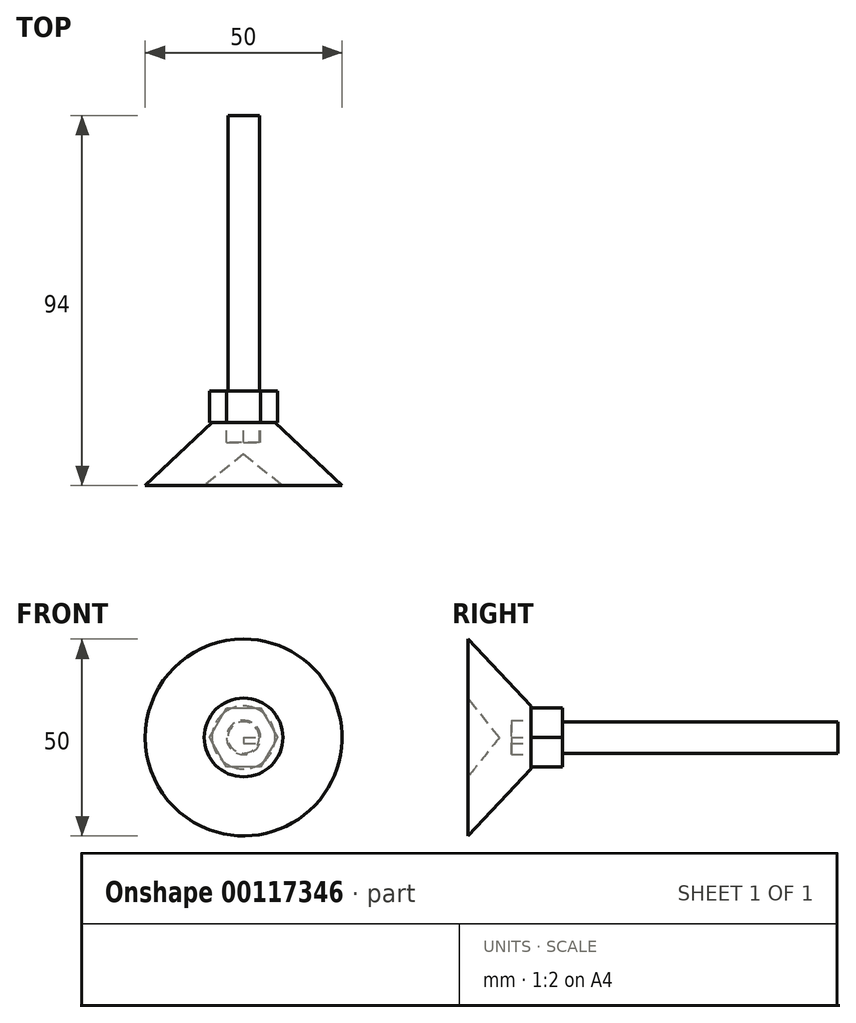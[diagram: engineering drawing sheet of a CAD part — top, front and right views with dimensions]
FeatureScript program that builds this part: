
annotation { "Feature Type Name" : "Feature", "Feature Type Description" : "" }
export const myFeature = defineFeature(function(context is Context, id is Id, definition is map)
    precondition{}
    {
        {
            var Q0;
            Q0=qCreatedBy(makeId("Front.planeOp"),FACE);
            var sketch = newSketch(context, id + "F0", { "sketchPlane" : qUnion([Q0])});
            skCircle(sketch, "E0", {"center": v(0, 0) * mm, "radius": 4 * mm});
            skSolve(sketch);
        }
        {
            var Q0;
            Q0 = qSketchRegion(id + "F0", true);
            extrude(context, id + "F1", {"entities" : qUnion([Q0]), "depth" : 70 * mm});
        }
        {
            var Q0;
            Q0=makeQuery(id+"F1.opExtrude","CAP_FACE",FACE,{"disambiguationData":[OSD([sQuery(id+"F0.wireOp",EDGE,"E0")])],"isStart":false});
            var sketch = newSketch(context, id + "F2", { "sketchPlane" : qUnion([Q0])});
            skCircle(sketch, "E1.cCircle", {"center": v(0, 0) * mm, "radius": 7.5 * mm, "construction": true});
            skLineSegment(sketch, "E1.0", {"start": v(8.66, 0.01) * mm, "end": v(4.34, -7.5) * mm});
            skLineSegment(sketch, "E1.1", {"start": v(4.34, -7.5) * mm, "end": v(-4.32, -7.5) * mm});
            skLineSegment(sketch, "E1.2", {"start": v(-4.32, -7.5) * mm, "end": v(-8.66, -0.01) * mm});
            skLineSegment(sketch, "E1.3", {"start": v(-8.66, -0.01) * mm, "end": v(-4.34, 7.5) * mm});
            skLineSegment(sketch, "E1.4", {"start": v(-4.34, 7.5) * mm, "end": v(4.32, 7.5) * mm});
            skLineSegment(sketch, "E1.5", {"start": v(4.32, 7.5) * mm, "end": v(8.66, 0.01) * mm});
            skPoint(sketch, "E1.0.midPoint", {"position": v(6.5, -3.74) * mm});
            skSolve(sketch);
        }
        {
            var Q0;
            Q0 = qSketchRegion(id + "F2", true);
            extrude(context, id + "F3", {"entities" : qUnion([Q0]), "operationType" : NewBodyOperationType.ADD, "depth" : 8 * mm});
        }
        {
            var Q0;
            Q0=makeQuery(id+"F3.opExtrude","CAP_FACE",FACE,{"disambiguationData":[OSD([sQuery(id+"F2.wireOp",EDGE,"E1.0"),sQuery(id+"F2.wireOp",EDGE,"E1.1"),sQuery(id+"F2.wireOp",EDGE,"E1.2"),sQuery(id+"F2.wireOp",EDGE,"E1.3"),sQuery(id+"F2.wireOp",EDGE,"E1.4"),sQuery(id+"F2.wireOp",EDGE,"E1.5")])],"isStart":false});
            var sketch = newSketch(context, id + "F4", { "sketchPlane" : qUnion([Q0])});
            skLineSegment(sketch, "E2.bottom", {"start": v(0, 0) * mm, "end": v(4.34, 0) * mm});
            skLineSegment(sketch, "E2.top", {"start": v(0, -1.5) * mm, "end": v(4.34, -1.5) * mm});
            skLineSegment(sketch, "E2.left", {"start": v(0, 0) * mm, "end": v(0, -1.5) * mm});
            skLineSegment(sketch, "E2.right", {"start": v(4.34, 0) * mm, "end": v(4.34, -1.5) * mm});
            skSolve(sketch);
        }
        {
            var Q0;
            Q0 = qSketchRegion(id + "F4", true);
            extrude(context, id + "F5", {"entities" : qUnion([Q0]), "operationType" : NewBodyOperationType.ADD, "depth" : 5 * mm});
        }
        {
            var Q0;
            Q0=makeQuery(id+"F5.opExtrude","SWEPT_FACE",FACE,{"disambiguationData":[OSD([sQuery(id+"F4.wireOp",EDGE,"E2.bottom")])]});
            var sketch = newSketch(context, id + "F6", { "sketchPlane" : qUnion([Q0])});
            skLineSegment(sketch, "E3", {"start": v(0, -78) * mm, "end": v(0, -94) * mm});
            skLineSegment(sketch, "E4", {"start": v(0, -78) * mm, "end": v(8, -78) * mm});
            skLineSegment(sketch, "E5", {"start": v(8, -78) * mm, "end": v(25, -94) * mm});
            skLineSegment(sketch, "E6", {"start": v(25, -94) * mm, "end": v(10, -94) * mm});
            skLineSegment(sketch, "E7", {"start": v(0, -86) * mm, "end": v(10, -94) * mm});
            skLineSegment(sketch, "E8", {"start": v(0, -86) * mm, "end": v(0, -78) * mm});
            skSolve(sketch);
        }
        {
            var Q0;
            {var subQ1=sQuery(id+"F6.wireOp",EDGE,"E5");Q0=makeQuery(id+"F6.imprint","IMPRINT",FACE,{"disambiguationData":[TD([[makeQuery(id+"F6.imprint","IMPRINT",EDGE,{"derivedFrom":subQ1}),-1.0]])]});}
            var Q1;
            Q1=sQuery(id+"F6.wireOp",EDGE,"E3");
            revolve(context, id + "F7", {"operationType" : NewBodyOperationType.ADD, "entities" : qUnion([Q0]), "axis" : qUnion([Q1]), "revolveType" : RevolveType.FULL});
        }
    });
